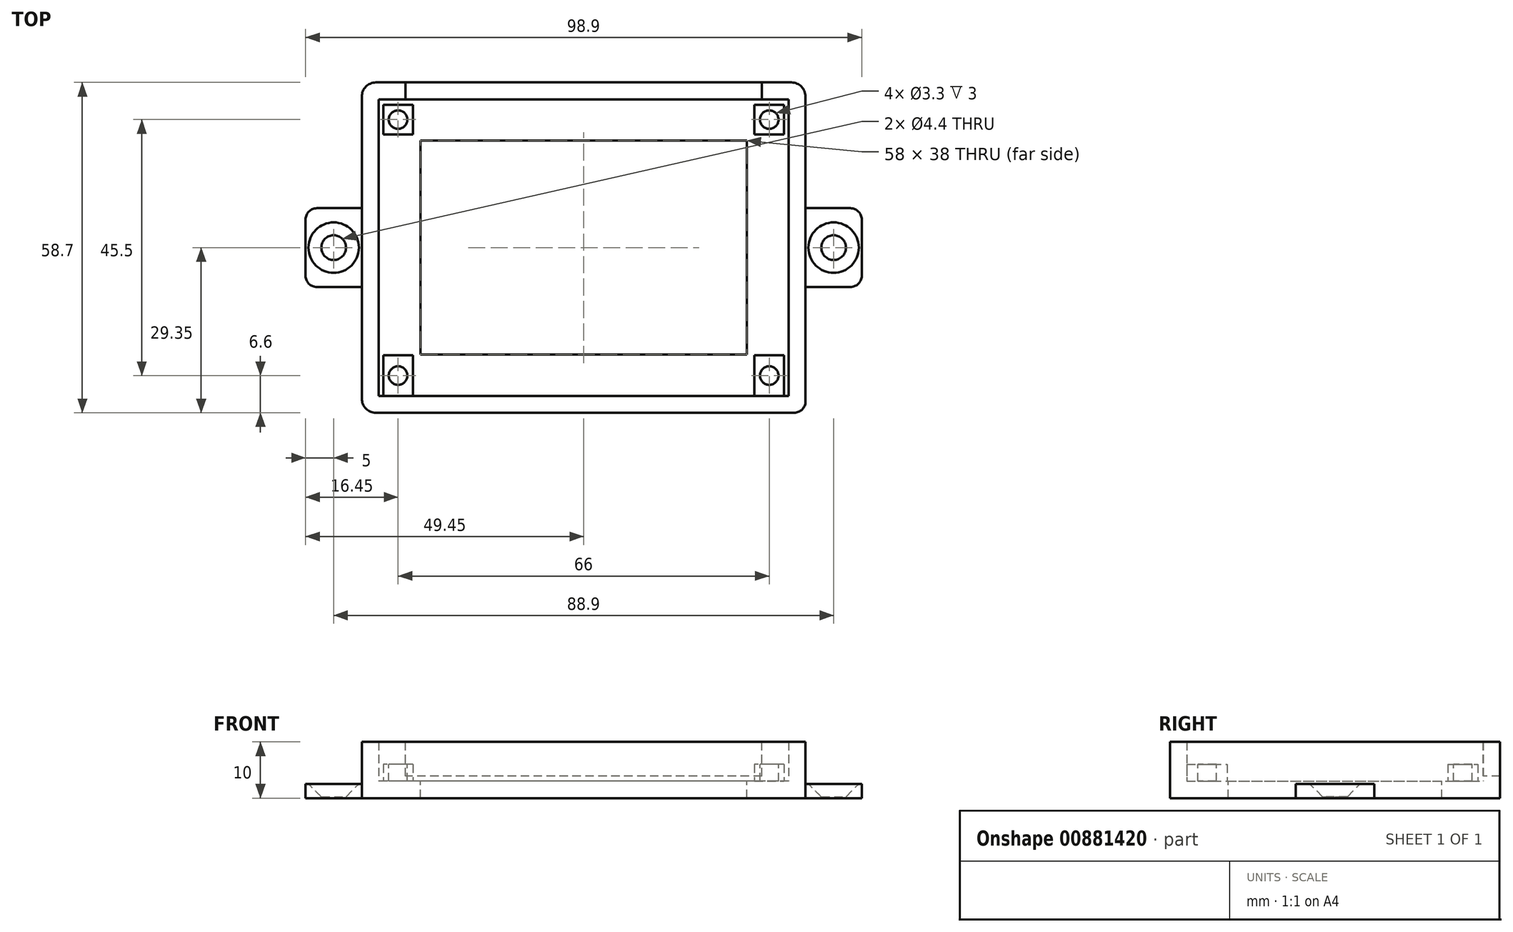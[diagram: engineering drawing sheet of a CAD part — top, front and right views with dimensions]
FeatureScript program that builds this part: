
annotation { "Feature Type Name" : "Feature", "Feature Type Description" : "" }
export const myFeature = defineFeature(function(context is Context, id is Id, definition is map)
    precondition{}
    {
        {
            var Q0;
            Q0=qCreatedBy(makeId("Top.planeOp"),FACE);
            var sketch = newSketch(context, id + "F0", { "sketchPlane" : qUnion([Q0])});
            skLineSegment(sketch, "E0.bottom", {"start": v(39.45, -29.35) * mm, "end": v(-39.45, -29.35) * mm});
            skLineSegment(sketch, "E0.top", {"start": v(39.45, 29.35) * mm, "end": v(-39.45, 29.35) * mm});
            skLineSegment(sketch, "E0.left", {"start": v(39.45, -29.35) * mm, "end": v(39.45, 29.35) * mm});
            skLineSegment(sketch, "E0.right", {"start": v(-39.45, -29.35) * mm, "end": v(-39.45, 29.35) * mm});
            skPoint(sketch, "E0.middle", {"position": v(0, 0) * mm});
            skSolve(sketch);
        }
        {
            var Q0;
            Q0=makeQuery(id+"F0.imprint","IMPRINT",FACE,{"disambiguationData":[TD([[makeQuery(id+"F0.imprint","IMPRINT",EDGE,{"derivedFrom":sQuery(id+"F0.wireOp",EDGE,"E0.bottom")}),-1.0]])]});
            extrude(context, id + "F1", {"entities" : qUnion([Q0]), "depth" : 10 * mm, "offsetDistance" : 25 * mm});
        }
        {
            var Q0;
            Q0=makeQuery(id+"F1.opExtrude","CAP_FACE",FACE,{"disambiguationData":[OSD([sQuery(id+"F0.wireOp",EDGE,"E0.bottom"),sQuery(id+"F0.wireOp",EDGE,"E0.top"),sQuery(id+"F0.wireOp",EDGE,"E0.left"),sQuery(id+"F0.wireOp",EDGE,"E0.right")])],"isStart":false});
            shell(context, id + "F2", {"entities" : qUnion([Q0]), "thickness" : 3 * mm});
        }
        {
            var Q0;
            Q0=makeQuery(id+"F1.opExtrude","SWEPT_FACE",FACE,{"disambiguationData":[OSD([sQuery(id+"F0.wireOp",EDGE,"E0.right")])]});
            var sketch = newSketch(context, id + "F3", { "sketchPlane" : qUnion([Q0])});
            skPoint(sketch, "E1", {"position": v(-7, 0) * mm});
            skPoint(sketch, "E2", {"position": v(7, 0) * mm});
            skPoint(sketch, "E3", {"position": v(7, 2.5) * mm});
            skPoint(sketch, "E4", {"position": v(-7, 2.5) * mm});
            skLineSegment(sketch, "E5", {"start": v(-7, 0) * mm, "end": v(-7, 2.5) * mm});
            skLineSegment(sketch, "E6", {"start": v(-7, 2.5) * mm, "end": v(7, 2.5) * mm});
            skLineSegment(sketch, "E7", {"start": v(7, 2.5) * mm, "end": v(7, 0) * mm});
            skLineSegment(sketch, "E8", {"start": v(7, 0) * mm, "end": v(-7, 0) * mm});
            skSolve(sketch);
        }
        {
            var Q0;
            Q0=makeQuery(id+"F3.imprint","IMPRINT",FACE,{"disambiguationData":[TD([[makeQuery(id+"F3.imprint","IMPRINT",EDGE,{"derivedFrom":sQuery(id+"F3.wireOp",EDGE,"E5")}),-1.0]])]});
            extrude(context, id + "F4", {"entities" : qUnion([Q0]), "operationType" : NewBodyOperationType.ADD, "depth" : 10 * mm, "offsetDistance" : 25 * mm});
        }
        {
            var Q0;
            Q0=makeQuery(id+"F4.opExtrude","SWEPT_FACE",FACE,{"disambiguationData":[OSD([sQuery(id+"F3.wireOp",EDGE,"E6")])]});
            var sketch = newSketch(context, id + "F5", { "sketchPlane" : qUnion([Q0])});
            skPoint(sketch, "E9", {"position": v(-44.45, 0) * mm});
            skPoint(sketch, "E9.positionSnap0", {"position": v(-44.45, -7) * mm});
            skSolve(sketch);
        }
        {
            var Q0;
            Q0=sQuery(id+"F5.wireOp",VERTEX,"E9");
            var Q1;
            Q1=makeQuery(id+"F1.opExtrude","SWEPT_BODY",BODY,{"disambiguationData":[OSD([sQuery(id+"F0.wireOp",EDGE,"E0.bottom"),sQuery(id+"F0.wireOp",EDGE,"E0.top"),sQuery(id+"F0.wireOp",EDGE,"E0.left"),sQuery(id+"F0.wireOp",EDGE,"E0.right")])]});
            hole(context, id + "F6", {"style" : HoleStyle.C_SINK, "endStyle" : HoleEndStyle.BLIND, "standardTappedOrClearance" : lookupTablePath({ "fit" : "Normal", "standard" : "ISO", "size" : "M4", "type" : "Clearance" }), "standardBlindInLast" : lookupTablePath({ "fit" : "Standard", "standard" : "ISO", "size" : "M4", "type" : "Clearance" }), "holeDiameter" : 4.4 * mm, "cSinkDiameter" : 8.96 * mm, "cSinkAngle" : 90 * degree, "majorDiameter" : 5 * mm, "holeDepth" : 5 * mm, "isTappedThrough" : true, "tappedDepth" : 12 * mm, "tapClearance" : 3, "locations" : qUnion([Q0]), "scope" : qUnion([Q1]), "startStyle" : HoleStartStyle.SKETCH});
        }
        {
            var Q0;
            Q0=makeQuery(id+"F1.opExtrude","SWEPT_FACE",FACE,{"disambiguationData":[OSD([sQuery(id+"F0.wireOp",EDGE,"E0.left")])]});
            var sketch = newSketch(context, id + "F7", { "sketchPlane" : qUnion([Q0])});
            skPoint(sketch, "E10", {"position": v(7, 0) * mm});
            skPoint(sketch, "E11", {"position": v(7, 2.5) * mm});
            skPoint(sketch, "E12", {"position": v(-6.1, 2.5) * mm});
            skPoint(sketch, "E13", {"position": v(-7, 0) * mm});
            skPoint(sketch, "E14", {"position": v(-7, 2.5) * mm});
            skLineSegment(sketch, "E15", {"start": v(-7, 0) * mm, "end": v(-7, 2.5) * mm});
            skLineSegment(sketch, "E16", {"start": v(-7, 2.5) * mm, "end": v(7, 2.5) * mm});
            skLineSegment(sketch, "E17", {"start": v(7, 2.5) * mm, "end": v(7, 0) * mm});
            skLineSegment(sketch, "E18", {"start": v(7, 0) * mm, "end": v(-7, 0) * mm});
            skSolve(sketch);
        }
        {
            var Q0;
            Q0=makeQuery(id+"F7.imprint","IMPRINT",FACE,{"disambiguationData":[TD([[makeQuery(id+"F7.imprint","IMPRINT",EDGE,{"derivedFrom":sQuery(id+"F7.wireOp",EDGE,"E15")}),-1.0]])]});
            extrude(context, id + "F8", {"entities" : qUnion([Q0]), "operationType" : NewBodyOperationType.ADD, "depth" : 10 * mm, "offsetDistance" : 25 * mm});
        }
        {
            var Q0;
            Q0=makeQuery(id+"F8.opExtrude","SWEPT_FACE",FACE,{"disambiguationData":[OSD([sQuery(id+"F7.wireOp",EDGE,"E16")])]});
            var sketch = newSketch(context, id + "F9", { "sketchPlane" : qUnion([Q0])});
            skPoint(sketch, "E19", {"position": v(44.45, 0) * mm});
            skPoint(sketch, "E19.positionSnap0", {"position": v(44.45, 7) * mm});
            skSolve(sketch);
        }
        {
            var Q0;
            Q0=sQuery(id+"F9.wireOp",VERTEX,"E19");
            var Q1;
            Q1=makeQuery(id+"F1.opExtrude","SWEPT_BODY",BODY,{"disambiguationData":[OSD([sQuery(id+"F0.wireOp",EDGE,"E0.bottom"),sQuery(id+"F0.wireOp",EDGE,"E0.top"),sQuery(id+"F0.wireOp",EDGE,"E0.left"),sQuery(id+"F0.wireOp",EDGE,"E0.right")])]});
            hole(context, id + "F10", {"style" : HoleStyle.C_SINK, "endStyle" : HoleEndStyle.BLIND, "standardTappedOrClearance" : lookupTablePath({ "fit" : "Normal", "standard" : "ISO", "size" : "M4", "type" : "Clearance" }), "standardBlindInLast" : lookupTablePath({ "fit" : "Standard", "standard" : "ISO", "size" : "M4", "type" : "Clearance" }), "holeDiameter" : 4.4 * mm, "cSinkDiameter" : 8.96 * mm, "cSinkAngle" : 90 * degree, "majorDiameter" : 5 * mm, "holeDepth" : 5 * mm, "isTappedThrough" : true, "tappedDepth" : 12 * mm, "tapClearance" : 3, "locations" : qUnion([Q0]), "scope" : qUnion([Q1]), "startStyle" : HoleStartStyle.SKETCH});
        }
        {
            var Q0;
            Q0=makeQuery(id+"F8.opExtrude","CAP_EDGE",EDGE,{"disambiguationData":[OSD([sQuery(id+"F7.wireOp",EDGE,"E17")])],"isStart":false});
            var Q1;
            Q1=makeQuery(id+"F8.opExtrude","CAP_EDGE",EDGE,{"disambiguationData":[OSD([sQuery(id+"F7.wireOp",EDGE,"E15")])],"isStart":false});
            var Q2;
            Q2=makeQuery(id+"F1.opExtrude","SWEPT_EDGE",EDGE,{"disambiguationData":[OSD([sQuery(id+"F0.wireOp",EDGE,"E0.bottom"),sQuery(id+"F0.wireOp",EDGE,"E0.left")])]});
            var Q3;
            Q3=makeQuery(id+"F4.opExtrude","CAP_EDGE",EDGE,{"disambiguationData":[OSD([sQuery(id+"F3.wireOp",EDGE,"E7")])],"isStart":false});
            var Q4;
            Q4=makeQuery(id+"F4.opExtrude","CAP_EDGE",EDGE,{"disambiguationData":[OSD([sQuery(id+"F3.wireOp",EDGE,"E5")])],"isStart":false});
            var Q5;
            Q5=makeQuery(id+"F4.opExtrude","CAP_EDGE",EDGE,{"disambiguationData":[OSD([sQuery(id+"F3.wireOp",EDGE,"E6")])],"isStart":true});
            var Q6;
            Q6=makeQuery(id+"F8.opExtrude","CAP_EDGE",EDGE,{"disambiguationData":[OSD([sQuery(id+"F7.wireOp",EDGE,"E16")])],"isStart":true});
            var Q7;
            Q7=makeQuery(id+"FhyoCYrS1Bowc3u_1.boolean.opBoolean","COPY",EDGE,{"derivedFrom":makeQuery(id+"FhyoCYrS1Bowc3u_1.opExtrude","CAP_EDGE",EDGE,{"disambiguationData":[OSD([sQuery(id+"FGxg2BuKLAHC74k_1.wireOp",EDGE,"KadDc5jr-7gxr-Imqz-lQ7y-f1avplHygi5P")])],"isStart":false})});
            var Q8;
            Q8=makeQuery(id+"FhyoCYrS1Bowc3u_1.boolean.opBoolean","COPY",EDGE,{"derivedFrom":makeQuery(id+"FhyoCYrS1Bowc3u_1.opExtrude","CAP_EDGE",EDGE,{"disambiguationData":[OSD([sQuery(id+"FGxg2BuKLAHC74k_1.wireOp",EDGE,"70z1bua5-r6vS-Akfn-fTIQ-XT4UpiJ0ouNG")])],"isStart":false})});
            var Q9;
            Q9=makeQuery(id+"FhyoCYrS1Bowc3u_1.boolean.opBoolean","COPY",EDGE,{"derivedFrom":makeQuery(id+"FhyoCYrS1Bowc3u_1.opExtrude","CAP_EDGE",EDGE,{"disambiguationData":[OSD([sQuery(id+"FGxg2BuKLAHC74k_1.wireOp",EDGE,"ITGG9AGb-pcH4-HS7s-pwSs-u8ssP1IFEGTD")])],"isStart":false})});
            var Q10;
            Q10=makeQuery(id+"FhyoCYrS1Bowc3u_1.boolean.opBoolean","COPY",EDGE,{"derivedFrom":makeQuery(id+"FhyoCYrS1Bowc3u_1.opExtrude","CAP_EDGE",EDGE,{"disambiguationData":[OSD([sQuery(id+"FGxg2BuKLAHC74k_1.wireOp",EDGE,"MHhLk95I-CgYu-bsYX-7dcV-dd8abfushh0y")])],"isStart":false})});
            fillet(context, id + "F11", {"entities" : qUnion([Q0, Q1, Q2, Q3, Q4, Q5, Q6, Q7, Q8, Q9, Q10]), "radius" : 2 * mm, "tangentPropagation" : true, "allowEdgeOverflow" : false});
        }
        {
            var Q0;
            Q0=makeQuery(id+"F1.opExtrude","CAP_FACE",FACE,{"disambiguationData":[OSD([sQuery(id+"F0.wireOp",EDGE,"E0.bottom"),sQuery(id+"F0.wireOp",EDGE,"E0.top"),sQuery(id+"F0.wireOp",EDGE,"E0.left"),sQuery(id+"F0.wireOp",EDGE,"E0.right")])],"isStart":false});
            var sketch = newSketch(context, id + "F12", { "sketchPlane" : qUnion([Q0])});
            skPoint(sketch, "E20", {"position": v(0, 29.35) * mm});
            skPoint(sketch, "E21", {"position": v(31.7, 29.35) * mm});
            skPoint(sketch, "E22", {"position": v(-31.7, 29.35) * mm});
            skPoint(sketch, "E23", {"position": v(-31.7, 26.35) * mm});
            skPoint(sketch, "E24", {"position": v(31.7, 26.35) * mm});
            skLineSegment(sketch, "E25", {"start": v(-31.7, 29.35) * mm, "end": v(-31.7, 26.35) * mm});
            skLineSegment(sketch, "E26", {"start": v(31.7, 29.35) * mm, "end": v(31.7, 26.35) * mm});
            skSolve(sketch);
        }
        {
            var Q0;
            {var subQ0=sQuery(id+"F12.wireOp",EDGE,"E25");Q0=makeQuery(id+"F12.imprint","IMPRINT",FACE,{"disambiguationData":[TD([[makeQuery(id+"F12.imprint","IMPRINT",EDGE,{"derivedFrom":subQ0}),1.0]])]});}
            extrude(context, id + "F13", {"entities" : qUnion([Q0]), "operationType" : NewBodyOperationType.REMOVE, "oppositeDirection" : true, "depth" : 6.1 * mm, "offsetDistance" : 25 * mm});
        }
        {
            var Q0;
            Q0=makeQuery(id+"F2.opShell","OFFSET_FACE",FACE,{"disambiguationData":[OSD([sQuery(id+"F0.wireOp",EDGE,"E0.bottom"),sQuery(id+"F0.wireOp",EDGE,"E0.top"),sQuery(id+"F0.wireOp",EDGE,"E0.left"),sQuery(id+"F0.wireOp",EDGE,"E0.right")])]});
            var sketch = newSketch(context, id + "F14", { "sketchPlane" : qUnion([Q0])});
            skPoint(sketch, "E27", {"position": v(-33, 22.75) * mm});
            skPoint(sketch, "E28", {"position": v(-33, -22.75) * mm});
            skPoint(sketch, "E29", {"position": v(33, -22.75) * mm});
            skPoint(sketch, "E30", {"position": v(33, 22.75) * mm});
            skLineSegment(sketch, "E31.bottom", {"start": v(-30.35, 20.1) * mm, "end": v(-35.65, 20.1) * mm});
            skLineSegment(sketch, "E31.top", {"start": v(-30.35, 25.4) * mm, "end": v(-35.65, 25.4) * mm});
            skLineSegment(sketch, "E31.left", {"start": v(-30.35, 20.1) * mm, "end": v(-30.35, 25.4) * mm});
            skLineSegment(sketch, "E31.right", {"start": v(-35.65, 20.1) * mm, "end": v(-35.65, 25.4) * mm});
            skLineSegment(sketch, "E32.bottom", {"start": v(30.35, 20.1) * mm, "end": v(35.65, 20.1) * mm});
            skLineSegment(sketch, "E32.top", {"start": v(30.35, 25.4) * mm, "end": v(35.65, 25.4) * mm});
            skLineSegment(sketch, "E32.left", {"start": v(30.35, 20.1) * mm, "end": v(30.35, 25.4) * mm});
            skLineSegment(sketch, "E32.right", {"start": v(35.65, 20.1) * mm, "end": v(35.65, 25.4) * mm});
            skLineSegment(sketch, "E33.bottom", {"start": v(-30.35, -26.35) * mm, "end": v(-35.65, -26.35) * mm});
            skLineSegment(sketch, "E33.top", {"start": v(-30.35, -19.15) * mm, "end": v(-35.65, -19.15) * mm});
            skLineSegment(sketch, "E33.left", {"start": v(-30.35, -26.35) * mm, "end": v(-30.35, -19.15) * mm});
            skLineSegment(sketch, "E33.right", {"start": v(-35.65, -26.35) * mm, "end": v(-35.65, -19.15) * mm});
            skLineSegment(sketch, "E34.bottom", {"start": v(30.35, -26.35) * mm, "end": v(35.65, -26.35) * mm});
            skLineSegment(sketch, "E34.top", {"start": v(30.35, -19.15) * mm, "end": v(35.65, -19.15) * mm});
            skLineSegment(sketch, "E34.left", {"start": v(30.35, -26.35) * mm, "end": v(30.35, -19.15) * mm});
            skLineSegment(sketch, "E34.right", {"start": v(35.65, -26.35) * mm, "end": v(35.65, -19.15) * mm});
            skSolve(sketch);
        }
        {
            var Q0;
            Q0=makeQuery(id+"F14.imprint","IMPRINT",FACE,{"disambiguationData":[TD([[makeQuery(id+"F14.imprint","IMPRINT",EDGE,{"derivedFrom":sQuery(id+"F14.wireOp",EDGE,"E31.bottom")}),-1.0]])]});
            var Q1;
            Q1=makeQuery(id+"F14.imprint","IMPRINT",FACE,{"disambiguationData":[TD([[makeQuery(id+"F14.imprint","IMPRINT",EDGE,{"derivedFrom":sQuery(id+"F14.wireOp",EDGE,"E32.bottom")}),1.0]])]});
            var Q2;
            Q2=makeQuery(id+"F14.imprint","IMPRINT",FACE,{"disambiguationData":[TD([[makeQuery(id+"F14.imprint","IMPRINT",EDGE,{"derivedFrom":sQuery(id+"F14.wireOp",EDGE,"E33.bottom")}),-1.0]])]});
            var Q3;
            Q3=makeQuery(id+"F14.imprint","IMPRINT",FACE,{"disambiguationData":[TD([[makeQuery(id+"F14.imprint","IMPRINT",EDGE,{"derivedFrom":sQuery(id+"F14.wireOp",EDGE,"E34.bottom")}),-1.0]])]});
            extrude(context, id + "F15", {"entities" : qUnion([Q0, Q1, Q2, Q3]), "operationType" : NewBodyOperationType.ADD, "depth" : 3 * mm, "offsetDistance" : 25 * mm});
        }
        {
            var Q0;
            Q0=sQuery(id+"F14.wireOp",VERTEX,"E28");
            var Q1;
            Q1=sQuery(id+"F14.wireOp",VERTEX,"E27");
            var Q2;
            Q2=sQuery(id+"F14.wireOp",VERTEX,"E29");
            var Q3;
            Q3=sQuery(id+"F14.wireOp",VERTEX,"E30");
            var Q4;
            Q4=makeQuery(id+"F1.opExtrude","SWEPT_BODY",BODY,{"disambiguationData":[OSD([sQuery(id+"F0.wireOp",EDGE,"E0.bottom"),sQuery(id+"F0.wireOp",EDGE,"E0.top"),sQuery(id+"F0.wireOp",EDGE,"E0.left"),sQuery(id+"F0.wireOp",EDGE,"E0.right")])]});
            hole(context, id + "F16", {"style" : HoleStyle.SIMPLE, "endStyle" : HoleEndStyle.THROUGH, "oppositeDirection" : true, "standardTappedOrClearance" : lookupTablePath({ "fit" : "Normal", "standard" : "ISO", "size" : "M3", "type" : "Clearance" }), "standardBlindInLast" : lookupTablePath({ "fit" : "Standard", "standard" : "ISO", "size" : "M3", "type" : "Clearance" }), "holeDiameter" : 3.3 * mm, "majorDiameter" : 5 * mm, "isTappedThrough" : true, "tappedDepth" : 12 * mm, "tapClearance" : 3, "locations" : qUnion([Q0, Q1, Q2, Q3]), "scope" : qUnion([Q4]), "startStyle" : HoleStartStyle.SKETCH});
        }
        {
            var Q0;
            {var subQ4=sQuery(id+"F14.wireOp",EDGE,"E31.bottom");Q0=makeQuery(id+"F14.imprint","IMPRINT",FACE,{"disambiguationData":[TD([[makeQuery(id+"F14.imprint","IMPRINT",EDGE,{"derivedFrom":subQ4}),1.0]])]});}
            var sketch = newSketch(context, id + "F17", { "sketchPlane" : qUnion([Q0])});
            skPoint(sketch, "E35", {"position": v(0, 0) * mm});
            skPoint(sketch, "E36", {"position": v(0, 19) * mm});
            skPoint(sketch, "E37", {"position": v(0, -19) * mm});
            skPoint(sketch, "E38", {"position": v(-29, -19) * mm});
            skPoint(sketch, "E39", {"position": v(29, -19) * mm});
            skPoint(sketch, "E40", {"position": v(29, 19) * mm});
            skPoint(sketch, "E41", {"position": v(-29, 19) * mm});
            skLineSegment(sketch, "E42", {"start": v(-29, 19) * mm, "end": v(-29, -19) * mm});
            skLineSegment(sketch, "E43", {"start": v(-29, -19) * mm, "end": v(29, -19) * mm});
            skLineSegment(sketch, "E44", {"start": v(29, -19) * mm, "end": v(29, 19) * mm});
            skLineSegment(sketch, "E45", {"start": v(29, 19) * mm, "end": v(-29, 19) * mm});
            skSolve(sketch);
        }
        {
            var Q0;
            Q0=makeQuery(id+"F17.imprint","IMPRINT",FACE,{"disambiguationData":[TD([[makeQuery(id+"F17.imprint","IMPRINT",EDGE,{"derivedFrom":sQuery(id+"F17.wireOp",EDGE,"E42")}),1.0]])]});
            extrude(context, id + "F18", {"entities" : qUnion([Q0]), "operationType" : NewBodyOperationType.REMOVE, "oppositeDirection" : true, "depth" : 25 * mm, "offsetDistance" : 25 * mm});
        }
        {
            var Q0;
            Q0=makeQuery(id+"F1.opExtrude","SWEPT_EDGE",EDGE,{"disambiguationData":[OSD([sQuery(id+"F0.wireOp",EDGE,"E0.top"),sQuery(id+"F0.wireOp",EDGE,"E0.right")])]});
            var Q1;
            Q1=makeQuery(id+"F1.opExtrude","SWEPT_EDGE",EDGE,{"disambiguationData":[OSD([sQuery(id+"F0.wireOp",EDGE,"E0.bottom"),sQuery(id+"F0.wireOp",EDGE,"E0.right")])]});
            var Q2;
            {var subQ0=sQuery(id+"F0.wireOp",EDGE,"E0.left");Q2=makeQuery(id+"F11.opFillet","BLEND_EDGE",EDGE,{"blendedFrom":[makeQuery(id+"F1.opExtrude","SWEPT_EDGE",EDGE,{"disambiguationData":[OSD([sQuery(id+"F0.wireOp",EDGE,"E0.bottom"),subQ0])]}),makeQuery(id+"F1.opExtrude","SWEPT_FACE",FACE,{"disambiguationData":[OSD([subQ0])]})],"blendedInto":[makeQuery(id+"F1.opExtrude","SWEPT_FACE",FACE,{"disambiguationData":[OSD([subQ0])]})]});}
            var Q3;
            Q3=makeQuery(id+"F1.opExtrude","SWEPT_EDGE",EDGE,{"disambiguationData":[OSD([sQuery(id+"F0.wireOp",EDGE,"E0.top"),sQuery(id+"F0.wireOp",EDGE,"E0.left")])]});
            fillet(context, id + "F19", {"entities" : qUnion([Q0, Q1, Q2, Q3]), "radius" : 2.5 * mm, "tangentPropagation" : true, "allowEdgeOverflow" : false});
        }
    });
